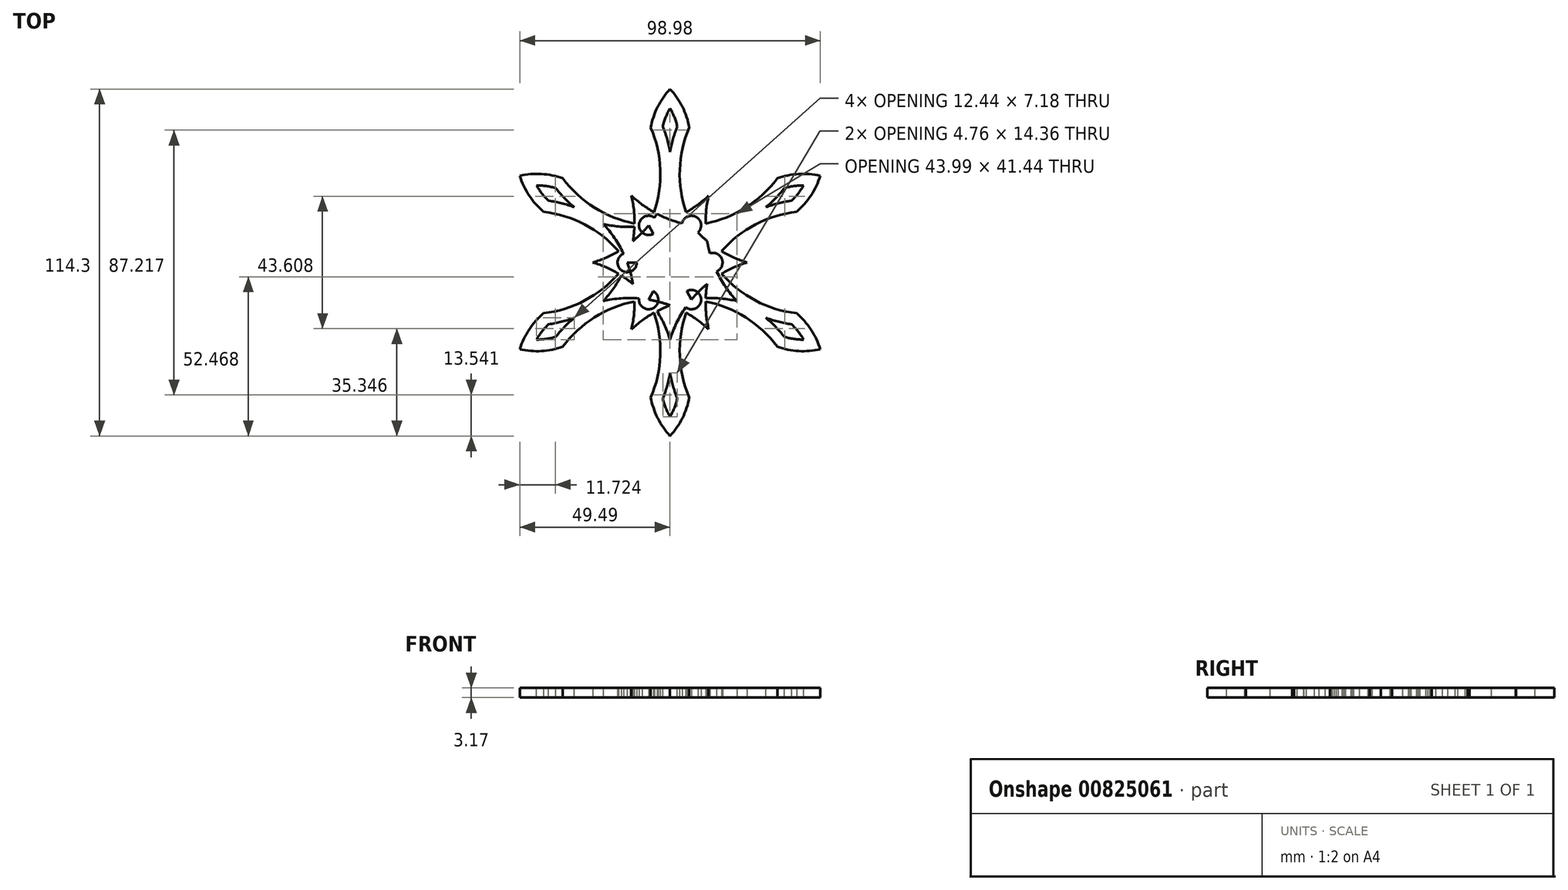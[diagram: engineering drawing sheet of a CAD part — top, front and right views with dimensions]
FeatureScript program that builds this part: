
annotation { "Feature Type Name" : "Feature", "Feature Type Description" : "" }
export const myFeature = defineFeature(function(context is Context, id is Id, definition is map)
    precondition{}
    {
        {
            var Q0;
            Q0=qCreatedBy(makeId("Top.planeOp"),FACE);
            var sketch = newSketch(context, id + "F0", { "sketchPlane" : qUnion([Q0])});
            skLineSegment(sketch, "E0", {"start": v(0, 0) * mm, "end": v(-18.31, 31.71) * mm});
            skLineSegment(sketch, "E1", {"start": v(0, 0) * mm, "end": v(17.16, 29.72) * mm});
            skArc(sketch, "E2", {"start": v(3.17, 5.5) * mm, "mid": v(0, 6.35) * mm, "end": v(-3.17, 5.5) * mm});
            skArc(sketch, "E3", {"start": v(0, 25.4) * mm, "mid": v(2.16, 19.88) * mm, "end": v(5.14, 14.76) * mm});
            skLineSegment(sketch, "E4", {"start": v(0, 44.45) * mm, "end": v(6.35, 44.45) * mm});
            skLineSegment(sketch, "E5", {"start": v(0, 44.45) * mm, "end": v(0, 57.15) * mm});
            skArc(sketch, "E6", {"start": v(6.35, 44.45) * mm, "mid": v(3.18, 29.85) * mm, "end": v(5.8, 15.14) * mm});
            skArc(sketch, "E7", {"start": v(6.35, 44.45) * mm, "mid": v(4.08, 51.25) * mm, "end": v(0, 57.15) * mm});
            skArc(sketch, "E8", {"start": v(5.8, 15.14) * mm, "mid": v(6.88, 9.06) * mm, "end": v(8.65, 14.98) * mm});
            skLineSegment(sketch, "E9.MirrorCS", {"start": v(0, 44.45) * mm, "end": v(-6.35, 44.45) * mm});
            skLineSegment(sketch, "E10.MirrorCS", {"start": v(0, 0) * mm, "end": v(18.31, 31.71) * mm});
            skLineSegment(sketch, "E11.MirrorCS", {"start": v(0, 0) * mm, "end": v(-17.16, 29.72) * mm});
            skArc(sketch, "E12.MirrorC", {"start": v(-3.17, 5.5) * mm, "mid": v(0, 6.35) * mm, "end": v(3.17, 5.5) * mm});
            skArc(sketch, "E13.MirrorCS", {"start": v(0, 25.4) * mm, "mid": v(-2.16, 19.88) * mm, "end": v(-5.14, 14.76) * mm});
            skArc(sketch, "E14.MirrorC", {"start": v(-5.8, 15.14) * mm, "mid": v(-6.88, 9.06) * mm, "end": v(-8.65, 14.98) * mm});
            skArc(sketch, "E15.MirrorCS", {"start": v(-6.35, 44.45) * mm, "mid": v(-3.18, 29.85) * mm, "end": v(-5.8, 15.14) * mm});
            skArc(sketch, "E16.MirrorCS", {"start": v(-6.35, 44.45) * mm, "mid": v(-4.08, 51.25) * mm, "end": v(0, 57.15) * mm});
            skArc(sketch, "E17.trimOffspring", {"start": v(7.06, 12.23) * mm, "mid": v(15.33, 4.76) * mm, "end": v(25.4, 0) * mm});
            skArc(sketch, "E18.trimOffspring", {"start": v(-7.06, 12.23) * mm, "mid": v(-15.33, 4.76) * mm, "end": v(-25.4, 0) * mm});
            skLineSegment(sketch, "E19.1.0", {"start": v(0, 0) * mm, "end": v(-34.32, 0) * mm});
            skArc(sketch, "E19.1.1", {"start": v(-41.67, 16.73) * mm, "mid": v(-27.44, 12.17) * mm, "end": v(-16, 2.55) * mm});
            skArc(sketch, "E19.1.2", {"start": v(-35.32, 27.72) * mm, "mid": v(-42.35, 29.16) * mm, "end": v(-49.5, 28.58) * mm});
            skArc(sketch, "E19.1.3", {"start": v(-7.06, 12.23) * mm, "mid": v(3.54, 15.65) * mm, "end": v(12.7, 22) * mm});
            skArc(sketch, "E19.1.4", {"start": v(-35.32, 27.72) * mm, "mid": v(-24.26, 17.68) * mm, "end": v(-10.21, 12.58) * mm});
            skLineSegment(sketch, "E19.1.5", {"start": v(-38.5, 22.23) * mm, "end": v(-49.5, 28.58) * mm});
            skLineSegment(sketch, "E19.1.8", {"start": v(0, 0) * mm, "end": v(-36.62, 0) * mm});
            skArc(sketch, "E19.1.9", {"start": v(-22, 12.7) * mm, "mid": v(-18.3, 8.07) * mm, "end": v(-15.35, 2.92) * mm});
            skArc(sketch, "E19.1.10", {"start": v(-41.67, 16.73) * mm, "mid": v(-46.43, 22.1) * mm, "end": v(-49.5, 28.57) * mm});
            skArc(sketch, "E19.1.11", {"start": v(-14.12, 0) * mm, "mid": v(-11.78, -10.9) * mm, "end": v(-12.7, -22) * mm});
            skArc(sketch, "E19.1.12", {"start": v(-10.21, 12.58) * mm, "mid": v(-4.4, 10.49) * mm, "end": v(-8.65, 14.98) * mm});
            skLineSegment(sketch, "E19.1.13", {"start": v(-38.5, 22.23) * mm, "end": v(-49.5, 28.58) * mm});
            skArc(sketch, "E19.1.14", {"start": v(-22, 12.7) * mm, "mid": v(-16.14, 11.8) * mm, "end": v(-10.2, 11.83) * mm});
            skArc(sketch, "E19.1.15", {"start": v(-3.18, 5.5) * mm, "mid": v(-5.5, 3.17) * mm, "end": v(-6.35, 0) * mm});
            skArc(sketch, "E19.1.16", {"start": v(-16, 2.55) * mm, "mid": v(-11.28, -1.43) * mm, "end": v(-17.3, 0) * mm});
            skLineSegment(sketch, "E19.1.17", {"start": v(-38.5, 22.23) * mm, "end": v(-41.67, 16.73) * mm});
            skLineSegment(sketch, "E19.1.18", {"start": v(-38.5, 22.23) * mm, "end": v(-35.32, 27.72) * mm});
            skArc(sketch, "E19.1.19", {"start": v(-6.35, 0) * mm, "mid": v(-5.5, 3.17) * mm, "end": v(-3.17, 5.5) * mm});
            skLineSegment(sketch, "E19.2.0", {"start": v(0, 0) * mm, "end": v(-17.16, -29.72) * mm});
            skArc(sketch, "E19.2.1", {"start": v(-35.32, -27.72) * mm, "mid": v(-24.26, -17.68) * mm, "end": v(-10.21, -12.58) * mm});
            skArc(sketch, "E19.2.2", {"start": v(-41.67, -16.73) * mm, "mid": v(-46.43, -22.1) * mm, "end": v(-49.5, -28.57) * mm});
            skArc(sketch, "E19.2.3", {"start": v(-14.12, 0) * mm, "mid": v(-11.78, 10.9) * mm, "end": v(-12.7, 22) * mm});
            skArc(sketch, "E19.2.4", {"start": v(-41.67, -16.73) * mm, "mid": v(-27.44, -12.17) * mm, "end": v(-16, -2.55) * mm});
            skLineSegment(sketch, "E19.2.5", {"start": v(-38.5, -22.22) * mm, "end": v(-49.5, -28.57) * mm});
            skLineSegment(sketch, "E19.2.6", {"start": v(0, 0) * mm, "end": v(-36.62, 0) * mm});
            skLineSegment(sketch, "E19.2.7", {"start": v(0, 0) * mm, "end": v(-34.32, 0) * mm});
            skLineSegment(sketch, "E19.2.8", {"start": v(0, 0) * mm, "end": v(-18.31, -31.71) * mm});
            skArc(sketch, "E19.2.9", {"start": v(-22, -12.7) * mm, "mid": v(-16.14, -11.8) * mm, "end": v(-10.2, -11.83) * mm});
            skArc(sketch, "E19.2.10", {"start": v(-35.32, -27.72) * mm, "mid": v(-42.35, -29.16) * mm, "end": v(-49.5, -28.57) * mm});
            skArc(sketch, "E19.2.11", {"start": v(-7.06, -12.23) * mm, "mid": v(3.54, -15.65) * mm, "end": v(12.7, -22) * mm});
            skArc(sketch, "E19.2.12", {"start": v(-16, -2.55) * mm, "mid": v(-11.28, 1.43) * mm, "end": v(-17.3, 0) * mm});
            skLineSegment(sketch, "E19.2.13", {"start": v(-38.5, -22.22) * mm, "end": v(-49.5, -28.57) * mm});
            skArc(sketch, "E19.2.14", {"start": v(-22, -12.7) * mm, "mid": v(-18.3, -8.07) * mm, "end": v(-15.35, -2.92) * mm});
            skArc(sketch, "E19.2.15", {"start": v(-6.35, 0) * mm, "mid": v(-5.5, -3.17) * mm, "end": v(-3.17, -5.5) * mm});
            skArc(sketch, "E19.2.16", {"start": v(-10.21, -12.58) * mm, "mid": v(-4.4, -10.49) * mm, "end": v(-8.65, -14.98) * mm});
            skLineSegment(sketch, "E19.2.17", {"start": v(-38.5, -22.22) * mm, "end": v(-35.32, -27.72) * mm});
            skLineSegment(sketch, "E19.2.18", {"start": v(-38.5, -22.22) * mm, "end": v(-41.67, -16.73) * mm});
            skArc(sketch, "E19.2.19", {"start": v(-3.18, -5.5) * mm, "mid": v(-5.5, -3.17) * mm, "end": v(-6.35, 0) * mm});
            skLineSegment(sketch, "E19.3.0", {"start": v(0, 0) * mm, "end": v(17.16, -29.72) * mm});
            skArc(sketch, "E19.3.1", {"start": v(6.35, -44.45) * mm, "mid": v(3.18, -29.85) * mm, "end": v(5.8, -15.14) * mm});
            skArc(sketch, "E19.3.2", {"start": v(-6.35, -44.45) * mm, "mid": v(-4.08, -51.25) * mm, "end": v(0, -57.15) * mm});
            skArc(sketch, "E19.3.3", {"start": v(-7.06, -12.23) * mm, "mid": v(-15.33, -4.76) * mm, "end": v(-25.4, 0) * mm});
            skArc(sketch, "E19.3.4", {"start": v(-6.35, -44.45) * mm, "mid": v(-3.18, -29.85) * mm, "end": v(-5.8, -15.14) * mm});
            skLineSegment(sketch, "E19.3.5", {"start": v(0, -44.45) * mm, "end": v(0, -57.15) * mm});
            skLineSegment(sketch, "E19.3.6", {"start": v(0, 0) * mm, "end": v(-18.31, -31.71) * mm});
            skLineSegment(sketch, "E19.3.7", {"start": v(0, 0) * mm, "end": v(-17.16, -29.72) * mm});
            skLineSegment(sketch, "E19.3.8", {"start": v(0, 0) * mm, "end": v(18.31, -31.71) * mm});
            skArc(sketch, "E19.3.9", {"start": v(0, -25.4) * mm, "mid": v(2.16, -19.88) * mm, "end": v(5.14, -14.76) * mm});
            skArc(sketch, "E19.3.10", {"start": v(6.35, -44.45) * mm, "mid": v(4.08, -51.25) * mm, "end": v(0, -57.15) * mm});
            skArc(sketch, "E19.3.11", {"start": v(7.06, -12.23) * mm, "mid": v(15.33, -4.76) * mm, "end": v(25.4, 0) * mm});
            skArc(sketch, "E19.3.12", {"start": v(-5.8, -15.14) * mm, "mid": v(-6.88, -9.06) * mm, "end": v(-8.65, -14.98) * mm});
            skLineSegment(sketch, "E19.3.13", {"start": v(0, -44.45) * mm, "end": v(0, -57.15) * mm});
            skArc(sketch, "E19.3.14", {"start": v(0, -25.4) * mm, "mid": v(-2.16, -19.88) * mm, "end": v(-5.14, -14.76) * mm});
            skArc(sketch, "E19.3.15", {"start": v(-3.17, -5.5) * mm, "mid": v(0, -6.35) * mm, "end": v(3.17, -5.5) * mm});
            skArc(sketch, "E19.3.16", {"start": v(5.8, -15.14) * mm, "mid": v(6.88, -9.06) * mm, "end": v(8.65, -14.98) * mm});
            skLineSegment(sketch, "E19.3.17", {"start": v(0, -44.45) * mm, "end": v(6.35, -44.45) * mm});
            skLineSegment(sketch, "E19.3.18", {"start": v(0, -44.45) * mm, "end": v(-6.35, -44.45) * mm});
            skArc(sketch, "E19.3.19", {"start": v(3.17, -5.5) * mm, "mid": v(0, -6.35) * mm, "end": v(-3.17, -5.5) * mm});
            skLineSegment(sketch, "E19.4.0", {"start": v(0, 0) * mm, "end": v(34.32, 0) * mm});
            skArc(sketch, "E19.4.1", {"start": v(41.67, -16.73) * mm, "mid": v(27.44, -12.17) * mm, "end": v(16, -2.55) * mm});
            skArc(sketch, "E19.4.2", {"start": v(35.32, -27.72) * mm, "mid": v(42.35, -29.16) * mm, "end": v(49.5, -28.58) * mm});
            skArc(sketch, "E19.4.3", {"start": v(7.06, -12.23) * mm, "mid": v(-3.54, -15.65) * mm, "end": v(-12.7, -22) * mm});
            skArc(sketch, "E19.4.4", {"start": v(35.32, -27.72) * mm, "mid": v(24.26, -17.68) * mm, "end": v(10.21, -12.58) * mm});
            skLineSegment(sketch, "E19.4.5", {"start": v(38.5, -22.23) * mm, "end": v(49.5, -28.58) * mm});
            skLineSegment(sketch, "E19.4.6", {"start": v(0, 0) * mm, "end": v(18.31, -31.71) * mm});
            skLineSegment(sketch, "E19.4.7", {"start": v(0, 0) * mm, "end": v(17.16, -29.72) * mm});
            skLineSegment(sketch, "E19.4.8", {"start": v(0, 0) * mm, "end": v(36.62, 0) * mm});
            skArc(sketch, "E19.4.9", {"start": v(22, -12.7) * mm, "mid": v(18.3, -8.07) * mm, "end": v(15.35, -2.92) * mm});
            skArc(sketch, "E19.4.10", {"start": v(41.67, -16.73) * mm, "mid": v(46.43, -22.1) * mm, "end": v(49.5, -28.58) * mm});
            skArc(sketch, "E19.4.11", {"start": v(14.12, 0) * mm, "mid": v(11.78, 10.9) * mm, "end": v(12.7, 22) * mm});
            skArc(sketch, "E19.4.12", {"start": v(10.21, -12.58) * mm, "mid": v(4.4, -10.49) * mm, "end": v(8.65, -14.98) * mm});
            skLineSegment(sketch, "E19.4.13", {"start": v(38.5, -22.23) * mm, "end": v(49.5, -28.58) * mm});
            skArc(sketch, "E19.4.14", {"start": v(22, -12.7) * mm, "mid": v(16.14, -11.8) * mm, "end": v(10.2, -11.83) * mm});
            skArc(sketch, "E19.4.15", {"start": v(3.17, -5.5) * mm, "mid": v(5.5, -3.18) * mm, "end": v(6.35, 0) * mm});
            skArc(sketch, "E19.4.16", {"start": v(16, -2.55) * mm, "mid": v(11.28, 1.43) * mm, "end": v(17.3, 0) * mm});
            skLineSegment(sketch, "E19.4.17", {"start": v(38.5, -22.23) * mm, "end": v(41.67, -16.73) * mm});
            skLineSegment(sketch, "E19.4.18", {"start": v(38.5, -22.23) * mm, "end": v(35.32, -27.72) * mm});
            skArc(sketch, "E19.4.19", {"start": v(6.35, 0) * mm, "mid": v(5.5, -3.17) * mm, "end": v(3.17, -5.5) * mm});
            skArc(sketch, "E19.5.1", {"start": v(35.32, 27.72) * mm, "mid": v(24.26, 17.68) * mm, "end": v(10.21, 12.58) * mm});
            skArc(sketch, "E19.5.2", {"start": v(41.67, 16.73) * mm, "mid": v(46.43, 22.1) * mm, "end": v(49.5, 28.57) * mm});
            skArc(sketch, "E19.5.3", {"start": v(14.12, 0) * mm, "mid": v(11.78, -10.9) * mm, "end": v(12.7, -22) * mm});
            skArc(sketch, "E19.5.4", {"start": v(41.67, 16.73) * mm, "mid": v(27.44, 12.17) * mm, "end": v(16, 2.55) * mm});
            skLineSegment(sketch, "E19.5.5", {"start": v(38.5, 22.23) * mm, "end": v(49.5, 28.58) * mm});
            skLineSegment(sketch, "E19.5.6", {"start": v(0, 0) * mm, "end": v(36.62, 0) * mm});
            skLineSegment(sketch, "E19.5.7", {"start": v(0, 0) * mm, "end": v(34.32, 0) * mm});
            skArc(sketch, "E19.5.9", {"start": v(22, 12.7) * mm, "mid": v(16.14, 11.8) * mm, "end": v(10.2, 11.83) * mm});
            skArc(sketch, "E19.5.10", {"start": v(35.32, 27.72) * mm, "mid": v(42.35, 29.16) * mm, "end": v(49.5, 28.58) * mm});
            skArc(sketch, "E19.5.11", {"start": v(7.06, 12.23) * mm, "mid": v(-3.54, 15.65) * mm, "end": v(-12.7, 22) * mm});
            skArc(sketch, "E19.5.12", {"start": v(16, 2.55) * mm, "mid": v(11.28, -1.43) * mm, "end": v(17.3, 0) * mm});
            skLineSegment(sketch, "E19.5.13", {"start": v(38.5, 22.23) * mm, "end": v(49.5, 28.58) * mm});
            skArc(sketch, "E19.5.14", {"start": v(22, 12.7) * mm, "mid": v(18.3, 8.07) * mm, "end": v(15.35, 2.92) * mm});
            skArc(sketch, "E19.5.15", {"start": v(6.35, 0) * mm, "mid": v(5.5, 3.17) * mm, "end": v(3.17, 5.5) * mm});
            skArc(sketch, "E19.5.16", {"start": v(10.21, 12.58) * mm, "mid": v(4.4, 10.49) * mm, "end": v(8.65, 14.98) * mm});
            skLineSegment(sketch, "E19.5.17", {"start": v(38.5, 22.23) * mm, "end": v(35.32, 27.72) * mm});
            skLineSegment(sketch, "E19.5.18", {"start": v(38.5, 22.23) * mm, "end": v(41.67, 16.73) * mm});
            skArc(sketch, "E19.5.19", {"start": v(3.17, 5.5) * mm, "mid": v(5.5, 3.17) * mm, "end": v(6.35, 0) * mm});
            skSolve(sketch);
        }
        {
            var Q0;
            Q0 = qSketchRegion(id + "F0", true);
            var Q1;
            {var subQ0=sQuery(id+"F0.wireOp",EDGE,"E19.3.3");var subQ1=sQuery(id+"F0.wireOp",EDGE,"E19.1.11");var subQ2=makeQuery(id+"F0.imprint","INTERSECT",VERTEX,{"derivedFrom":[subQ1,subQ0]});Q1=makeQuery(id+"F0.imprint","IMPRINT",FACE,{"disambiguationData":[TD([[makeQuery(id+"F0.imprint","IMPRINT",EDGE,{"disambiguationData":[TD([[subQ2,-1.0]])],"derivedFrom":subQ1}),1.0]])]});}
            var Q2;
            {var subQ0=sQuery(id+"F0.wireOp",EDGE,"E19.2.12");var subQ1=sQuery(id+"F0.wireOp",EDGE,"E19.1.11");var subQ2=makeQuery(id+"F0.imprint","INTERSECT",VERTEX,{"derivedFrom":[subQ1,subQ0]});Q2=makeQuery(id+"F0.imprint","IMPRINT",FACE,{"disambiguationData":[TD([[makeQuery(id+"F0.imprint","IMPRINT",EDGE,{"disambiguationData":[TD([[subQ2,-1.0]])],"derivedFrom":subQ1}),-1.0]])]});}
            var Q3;
            {var subQ0=sQuery(id+"F0.wireOp",EDGE,"E19.2.3");var subQ1=sQuery(id+"F0.wireOp",EDGE,"E18.trimOffspring");var subQ2=makeQuery(id+"F0.imprint","INTERSECT",VERTEX,{"derivedFrom":[subQ1,subQ0]});Q3=makeQuery(id+"F0.imprint","IMPRINT",FACE,{"disambiguationData":[TD([[makeQuery(id+"F0.imprint","IMPRINT",EDGE,{"disambiguationData":[TD([[subQ2,-1.0]])],"derivedFrom":subQ1}),1.0]])]});}
            var Q4;
            {var subQ0=sQuery(id+"F0.wireOp",EDGE,"E19.1.12");var subQ1=sQuery(id+"F0.wireOp",EDGE,"E18.trimOffspring");var subQ2=makeQuery(id+"F0.imprint","INTERSECT",VERTEX,{"derivedFrom":[subQ1,subQ0]});Q4=makeQuery(id+"F0.imprint","IMPRINT",FACE,{"disambiguationData":[TD([[makeQuery(id+"F0.imprint","IMPRINT",EDGE,{"disambiguationData":[TD([[subQ2,-1.0]])],"derivedFrom":subQ1}),-1.0]])]});}
            var Q5;
            {var subQ0=sQuery(id+"F0.wireOp",EDGE,"E19.3.12");var subQ1=sQuery(id+"F0.wireOp",EDGE,"E19.2.11");var subQ2=makeQuery(id+"F0.imprint","INTERSECT",VERTEX,{"derivedFrom":[subQ1,subQ0]});Q5=makeQuery(id+"F0.imprint","IMPRINT",FACE,{"disambiguationData":[TD([[makeQuery(id+"F0.imprint","IMPRINT",EDGE,{"disambiguationData":[TD([[subQ2,-1.0]])],"derivedFrom":subQ1}),-1.0]])]});}
            var Q6;
            {var subQ0=sQuery(id+"F0.wireOp",EDGE,"E19.4.3");var subQ1=sQuery(id+"F0.wireOp",EDGE,"E19.2.11");var subQ2=makeQuery(id+"F0.imprint","INTERSECT",VERTEX,{"derivedFrom":[subQ1,subQ0]});Q6=makeQuery(id+"F0.imprint","IMPRINT",FACE,{"disambiguationData":[TD([[makeQuery(id+"F0.imprint","IMPRINT",EDGE,{"disambiguationData":[TD([[subQ2,-1.0]])],"derivedFrom":subQ1}),1.0]])]});}
            var Q7;
            {var subQ0=sQuery(id+"F0.wireOp",EDGE,"E19.4.12");var subQ1=sQuery(id+"F0.wireOp",EDGE,"E19.3.11");var subQ2=makeQuery(id+"F0.imprint","INTERSECT",VERTEX,{"derivedFrom":[subQ1,subQ0]});Q7=makeQuery(id+"F0.imprint","IMPRINT",FACE,{"disambiguationData":[TD([[makeQuery(id+"F0.imprint","IMPRINT",EDGE,{"disambiguationData":[TD([[subQ2,-1.0]])],"derivedFrom":subQ1}),-1.0]])]});}
            var Q8;
            {var subQ0=sQuery(id+"F0.wireOp",EDGE,"E19.5.3");var subQ1=sQuery(id+"F0.wireOp",EDGE,"E19.3.11");var subQ2=makeQuery(id+"F0.imprint","INTERSECT",VERTEX,{"derivedFrom":[subQ1,subQ0]});Q8=makeQuery(id+"F0.imprint","IMPRINT",FACE,{"disambiguationData":[TD([[makeQuery(id+"F0.imprint","IMPRINT",EDGE,{"disambiguationData":[TD([[subQ2,-1.0]])],"derivedFrom":subQ1}),1.0]])]});}
            var Q9;
            {var subQ0=sQuery(id+"F0.wireOp",EDGE,"E19.4.11");var subQ1=sQuery(id+"F0.wireOp",EDGE,"E17.trimOffspring");var subQ2=makeQuery(id+"F0.imprint","INTERSECT",VERTEX,{"derivedFrom":[subQ1,subQ0]});Q9=makeQuery(id+"F0.imprint","IMPRINT",FACE,{"disambiguationData":[TD([[makeQuery(id+"F0.imprint","IMPRINT",EDGE,{"disambiguationData":[TD([[subQ2,-1.0]])],"derivedFrom":subQ1}),-1.0]])]});}
            var Q10;
            {var subQ0=sQuery(id+"F0.wireOp",EDGE,"E19.5.16");var subQ1=sQuery(id+"F0.wireOp",EDGE,"E17.trimOffspring");var subQ2=makeQuery(id+"F0.imprint","INTERSECT",VERTEX,{"derivedFrom":[subQ1,subQ0]});Q10=makeQuery(id+"F0.imprint","IMPRINT",FACE,{"disambiguationData":[TD([[makeQuery(id+"F0.imprint","IMPRINT",EDGE,{"disambiguationData":[TD([[subQ2,-1.0]])],"derivedFrom":subQ1}),1.0]])]});}
            var Q11;
            {var subQ0=sQuery(id+"F0.wireOp",EDGE,"E19.5.16");var subQ1=sQuery(id+"F0.wireOp",EDGE,"E3");var subQ2=makeQuery(id+"F0.imprint","INTERSECT",VERTEX,{"derivedFrom":[subQ1,subQ0]});Q11=makeQuery(id+"F0.imprint","IMPRINT",FACE,{"disambiguationData":[TD([[makeQuery(id+"F0.imprint","IMPRINT",EDGE,{"disambiguationData":[TD([[subQ2,1.0]])],"derivedFrom":subQ1}),-1.0]])]});}
            var Q12;
            {var subQ0=sQuery(id+"F0.wireOp",EDGE,"E19.1.12");var subQ1=sQuery(id+"F0.wireOp",EDGE,"E13.MirrorCS");var subQ2=makeQuery(id+"F0.imprint","INTERSECT",VERTEX,{"derivedFrom":[subQ1,subQ0]});Q12=makeQuery(id+"F0.imprint","IMPRINT",FACE,{"disambiguationData":[TD([[makeQuery(id+"F0.imprint","IMPRINT",EDGE,{"disambiguationData":[TD([[subQ2,1.0]])],"derivedFrom":subQ1}),1.0]])]});}
            var Q13;
            {var subQ5=sQuery(id+"F0.wireOp",EDGE,"E19.3.19");Q13=makeQuery(id+"F0.imprint","IMPRINT",FACE,{"disambiguationData":[TD([[makeQuery(id+"F0.imprint","IMPRINT",EDGE,{"derivedFrom":subQ5}),1.0]])]});}
            var Q14;
            {var subQ5=sQuery(id+"F0.wireOp",EDGE,"E19.4.19");Q14=makeQuery(id+"F0.imprint","IMPRINT",FACE,{"disambiguationData":[TD([[makeQuery(id+"F0.imprint","IMPRINT",EDGE,{"derivedFrom":subQ5}),1.0]])]});}
            var Q15;
            {var subQ0=sQuery(id+"F0.wireOp",EDGE,"E19.5.19");Q15=makeQuery(id+"F0.imprint","IMPRINT",FACE,{"disambiguationData":[TD([[makeQuery(id+"F0.imprint","IMPRINT",EDGE,{"derivedFrom":subQ0}),1.0]])]});}
            var Q16;
            {var subQ7=sQuery(id+"F0.wireOp",EDGE,"E12.MirrorC");Q16=makeQuery(id+"F0.imprint","IMPRINT",FACE,{"disambiguationData":[TD([[makeQuery(id+"F0.imprint","IMPRINT",EDGE,{"derivedFrom":subQ7}),1.0]])]});}
            var Q17;
            {var subQ5=sQuery(id+"F0.wireOp",EDGE,"E19.1.19");Q17=makeQuery(id+"F0.imprint","IMPRINT",FACE,{"disambiguationData":[TD([[makeQuery(id+"F0.imprint","IMPRINT",EDGE,{"derivedFrom":subQ5}),1.0]])]});}
            var Q18;
            {var subQ5=sQuery(id+"F0.wireOp",EDGE,"E19.2.19");Q18=makeQuery(id+"F0.imprint","IMPRINT",FACE,{"disambiguationData":[TD([[makeQuery(id+"F0.imprint","IMPRINT",EDGE,{"derivedFrom":subQ5}),1.0]])]});}
            extrude(context, id + "F1", {"entities" : qUnion([Q0, Q1, Q2, Q3, Q4, Q5, Q6, Q7, Q8, Q9, Q10, Q11, Q12, Q13, Q14, Q15, Q16, Q17, Q18]), "depth" : 3.17 * mm, "offsetDistance" : 25.4 * mm});
        }
        {
            var Q0;
            Q0=makeQuery(id+"F1.opExtrude","CAP_FACE",FACE,{"disambiguationData":[OSD([sQuery(id+"F0.wireOp",EDGE,"E3"),sQuery(id+"F0.wireOp",EDGE,"E6"),sQuery(id+"F0.wireOp",EDGE,"E7"),sQuery(id+"F0.wireOp",EDGE,"E8"),sQuery(id+"F0.wireOp",EDGE,"E12.MirrorC"),sQuery(id+"F0.wireOp",EDGE,"E13.MirrorCS"),sQuery(id+"F0.wireOp",EDGE,"E14.MirrorC"),sQuery(id+"F0.wireOp",EDGE,"E15.MirrorCS"),sQuery(id+"F0.wireOp",EDGE,"E16.MirrorCS"),sQuery(id+"F0.wireOp",EDGE,"E17.trimOffspring"),sQuery(id+"F0.wireOp",EDGE,"E18.trimOffspring"),sQuery(id+"F0.wireOp",EDGE,"E19.1.1"),sQuery(id+"F0.wireOp",EDGE,"E19.1.2"),sQuery(id+"F0.wireOp",EDGE,"E19.1.3"),sQuery(id+"F0.wireOp",EDGE,"E19.1.4"),sQuery(id+"F0.wireOp",EDGE,"E19.1.9"),sQuery(id+"F0.wireOp",EDGE,"E19.1.10"),sQuery(id+"F0.wireOp",EDGE,"E19.1.11"),sQuery(id+"F0.wireOp",EDGE,"E19.1.12"),sQuery(id+"F0.wireOp",EDGE,"E19.1.14"),sQuery(id+"F0.wireOp",EDGE,"E19.1.16"),sQuery(id+"F0.wireOp",EDGE,"E19.1.19"),sQuery(id+"F0.wireOp",EDGE,"E19.2.1"),sQuery(id+"F0.wireOp",EDGE,"E19.2.2"),sQuery(id+"F0.wireOp",EDGE,"E19.2.3"),sQuery(id+"F0.wireOp",EDGE,"E19.2.4"),sQuery(id+"F0.wireOp",EDGE,"E19.2.9"),sQuery(id+"F0.wireOp",EDGE,"E19.2.10"),sQuery(id+"F0.wireOp",EDGE,"E19.2.11"),sQuery(id+"F0.wireOp",EDGE,"E19.2.12"),sQuery(id+"F0.wireOp",EDGE,"E19.2.14"),sQuery(id+"F0.wireOp",EDGE,"E19.2.16"),sQuery(id+"F0.wireOp",EDGE,"E19.2.19"),sQuery(id+"F0.wireOp",EDGE,"E19.3.1"),sQuery(id+"F0.wireOp",EDGE,"E19.3.2"),sQuery(id+"F0.wireOp",EDGE,"E19.3.3"),sQuery(id+"F0.wireOp",EDGE,"E19.3.4"),sQuery(id+"F0.wireOp",EDGE,"E19.3.9"),sQuery(id+"F0.wireOp",EDGE,"E19.3.10"),sQuery(id+"F0.wireOp",EDGE,"E19.3.11"),sQuery(id+"F0.wireOp",EDGE,"E19.3.12"),sQuery(id+"F0.wireOp",EDGE,"E19.3.14"),sQuery(id+"F0.wireOp",EDGE,"E19.3.16"),sQuery(id+"F0.wireOp",EDGE,"E19.3.19"),sQuery(id+"F0.wireOp",EDGE,"E19.4.1"),sQuery(id+"F0.wireOp",EDGE,"E19.4.2"),sQuery(id+"F0.wireOp",EDGE,"E19.4.3"),sQuery(id+"F0.wireOp",EDGE,"E19.4.4"),sQuery(id+"F0.wireOp",EDGE,"E19.4.9"),sQuery(id+"F0.wireOp",EDGE,"E19.4.10"),sQuery(id+"F0.wireOp",EDGE,"E19.4.11"),sQuery(id+"F0.wireOp",EDGE,"E19.4.12"),sQuery(id+"F0.wireOp",EDGE,"E19.4.14"),sQuery(id+"F0.wireOp",EDGE,"E19.4.16"),sQuery(id+"F0.wireOp",EDGE,"E19.4.19"),sQuery(id+"F0.wireOp",EDGE,"E19.5.1"),sQuery(id+"F0.wireOp",EDGE,"E19.5.2"),sQuery(id+"F0.wireOp",EDGE,"E19.5.3"),sQuery(id+"F0.wireOp",EDGE,"E19.5.4"),sQuery(id+"F0.wireOp",EDGE,"E19.5.9"),sQuery(id+"F0.wireOp",EDGE,"E19.5.10"),sQuery(id+"F0.wireOp",EDGE,"E19.5.11"),sQuery(id+"F0.wireOp",EDGE,"E19.5.12"),sQuery(id+"F0.wireOp",EDGE,"E19.5.14"),sQuery(id+"F0.wireOp",EDGE,"E19.5.16"),sQuery(id+"F0.wireOp",EDGE,"E19.5.19")])],"isStart":false});
            var sketch = newSketch(context, id + "F2", { "sketchPlane" : qUnion([Q0])});
            skArc(sketch, "E20.3", {"start": v(37.63, 24.48) * mm, "mid": v(34.75, 21.19) * mm, "end": v(31.55, 18.21) * mm});
            skArc(sketch, "E20.4", {"start": v(43.99, 25.4) * mm, "mid": v(40.77, 25.17) * mm, "end": v(37.63, 24.48) * mm});
            skArc(sketch, "E20.5", {"start": v(40.01, 20.35) * mm, "mid": v(42.19, 22.72) * mm, "end": v(43.99, 25.4) * mm});
            skArc(sketch, "E20.9", {"start": v(40.01, -20.35) * mm, "mid": v(35.72, -19.5) * mm, "end": v(31.55, -18.21) * mm});
            skArc(sketch, "E20.10", {"start": v(43.99, -25.4) * mm, "mid": v(42.19, -22.72) * mm, "end": v(40.01, -20.35) * mm});
            skArc(sketch, "E20.11", {"start": v(2.38, 44.83) * mm, "mid": v(1.41, 47.9) * mm, "end": v(0, 50.8) * mm});
            skArc(sketch, "E20.12", {"start": v(37.63, -24.48) * mm, "mid": v(40.77, -25.17) * mm, "end": v(43.99, -25.4) * mm});
            skArc(sketch, "E20.16", {"start": v(-40.01, 20.35) * mm, "mid": v(-35.72, 19.5) * mm, "end": v(-31.55, 18.21) * mm});
            skArc(sketch, "E20.17", {"start": v(-43.99, 25.4) * mm, "mid": v(-42.19, 22.72) * mm, "end": v(-40.01, 20.35) * mm});
            skArc(sketch, "E20.18", {"start": v(-37.63, 24.48) * mm, "mid": v(-40.77, 25.17) * mm, "end": v(-43.99, 25.4) * mm});
            skArc(sketch, "E20.20", {"start": v(0, 50.8) * mm, "mid": v(-1.41, 47.9) * mm, "end": v(-2.38, 44.83) * mm});
            skArc(sketch, "E20.21", {"start": v(-2.38, 44.83) * mm, "mid": v(-0.97, 40.69) * mm, "end": v(0, 36.43) * mm});
            skArc(sketch, "E20.25", {"start": v(-40.01, -20.35) * mm, "mid": v(-42.19, -22.72) * mm, "end": v(-43.99, -25.4) * mm});
            skArc(sketch, "E20.26", {"start": v(-43.99, -25.4) * mm, "mid": v(-40.77, -25.17) * mm, "end": v(-37.63, -24.48) * mm});
            skArc(sketch, "E20.27", {"start": v(-37.63, -24.48) * mm, "mid": v(-34.75, -21.19) * mm, "end": v(-31.55, -18.21) * mm});
            skArc(sketch, "E20.31", {"start": v(-2.38, -44.83) * mm, "mid": v(-1.41, -47.9) * mm, "end": v(0, -50.8) * mm});
            skArc(sketch, "E20.32", {"start": v(0, -50.8) * mm, "mid": v(1.41, -47.9) * mm, "end": v(2.38, -44.83) * mm});
            skArc(sketch, "E20.33", {"start": v(2.38, -44.83) * mm, "mid": v(0.97, -40.69) * mm, "end": v(0, -36.43) * mm});
            skArc(sketch, "E21.trimOffspring", {"start": v(0, 36.43) * mm, "mid": v(0.97, 40.69) * mm, "end": v(2.38, 44.83) * mm});
            skArc(sketch, "E22.trimOffspring", {"start": v(31.55, 18.21) * mm, "mid": v(35.72, 19.5) * mm, "end": v(40.01, 20.35) * mm});
            skArc(sketch, "E23.trimOffspring", {"start": v(-31.55, 18.21) * mm, "mid": v(-34.75, 21.19) * mm, "end": v(-37.63, 24.48) * mm});
            skArc(sketch, "E24.trimOffspring", {"start": v(-31.55, -18.21) * mm, "mid": v(-35.72, -19.5) * mm, "end": v(-40.01, -20.35) * mm});
            skArc(sketch, "E25.trimOffspring", {"start": v(0, -36.43) * mm, "mid": v(-0.97, -40.69) * mm, "end": v(-2.38, -44.83) * mm});
            skArc(sketch, "E26.trimOffspring", {"start": v(31.55, -18.21) * mm, "mid": v(34.75, -21.19) * mm, "end": v(37.63, -24.48) * mm});
            skSolve(sketch);
        }
        {
            var Q0;
            Q0 = qSketchRegion(id + "F2", true);
            extrude(context, id + "F3", {"entities" : qUnion([Q0]), "operationType" : NewBodyOperationType.REMOVE, "oppositeDirection" : true, "depth" : 3.17 * mm, "offsetDistance" : 25.4 * mm});
        }
    });
